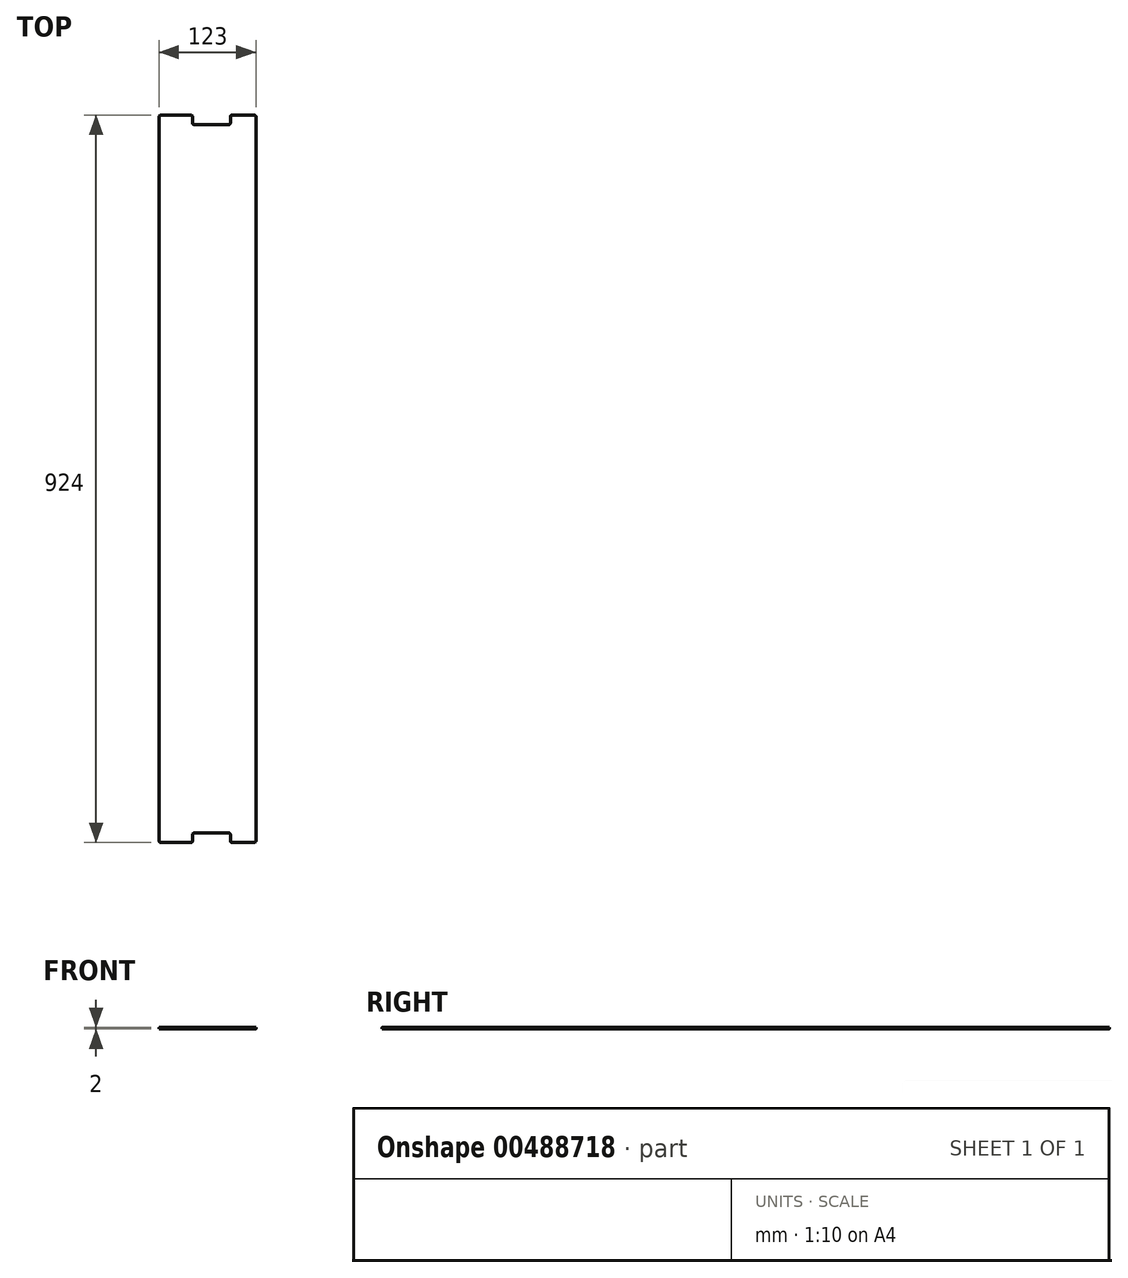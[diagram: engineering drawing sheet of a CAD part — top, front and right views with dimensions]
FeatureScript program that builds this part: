
annotation { "Feature Type Name" : "Feature", "Feature Type Description" : "" }
export const myFeature = defineFeature(function(context is Context, id is Id, definition is map)
    precondition{}
    {
        {
            var Q0;
            Q0=qCreatedBy(makeId("Top.planeOp"),FACE);
            var sketch = newSketch(context, id + "F0", { "sketchPlane" : qUnion([Q0])});
            skPoint(sketch, "E0.middle", {"position": v(0, 0) * mm});
            skLineSegment(sketch, "E1.bottom", {"start": v(24, 450) * mm, "end": v(-24, 450) * mm});
            skLineSegment(sketch, "E1.top", {"start": v(24, -450) * mm, "end": v(-24, -450) * mm});
            skLineSegment(sketch, "E1.left", {"start": v(24, 450) * mm, "end": v(24, -450) * mm});
            skLineSegment(sketch, "E1.right", {"start": v(-24, 450) * mm, "end": v(-24, -450) * mm});
            skLineSegment(sketch, "E2", {"start": v(-24, 450) * mm, "end": v(-24, 462) * mm});
            skLineSegment(sketch, "E3", {"start": v(-24, 462) * mm, "end": v(-66.5, 462) * mm});
            skLineSegment(sketch, "E4", {"start": v(-66.5, 462) * mm, "end": v(-66.5, -462) * mm});
            skLineSegment(sketch, "E5", {"start": v(24, 450) * mm, "end": v(24, 462) * mm});
            skLineSegment(sketch, "E6", {"start": v(24, 462) * mm, "end": v(56.5, 462) * mm});
            skLineSegment(sketch, "E7", {"start": v(56.5, 462) * mm, "end": v(56.5, -462) * mm});
            skLineSegment(sketch, "E8", {"start": v(56.5, -462) * mm, "end": v(24, -462) * mm});
            skLineSegment(sketch, "E9", {"start": v(24, -462) * mm, "end": v(24, -450) * mm});
            skLineSegment(sketch, "E10", {"start": v(-66.5, -462) * mm, "end": v(-24, -462) * mm});
            skLineSegment(sketch, "E11", {"start": v(-24, -462) * mm, "end": v(-24, -450) * mm});
            skSolve(sketch);
        }
        {
            var Q0;
            Q0=makeQuery(id+"F0.imprint","IMPRINT",FACE,{"disambiguationData":[TD([[makeQuery(id+"F0.imprint","IMPRINT",EDGE,{"derivedFrom":sQuery(id+"F0.wireOp",EDGE,"E1.bottom")}),1.0]])]});
            var Q1;
            Q1=makeQuery(id+"F0.imprint","IMPRINT",FACE,{"disambiguationData":[TD([[makeQuery(id+"F0.imprint","IMPRINT",EDGE,{"derivedFrom":sQuery(id+"F0.wireOp",EDGE,"E1.left")}),1.0]])]});
            var Q2;
            Q2=makeQuery(id+"F0.imprint","IMPRINT",FACE,{"disambiguationData":[TD([[makeQuery(id+"F0.imprint","IMPRINT",EDGE,{"derivedFrom":sQuery(id+"F0.wireOp",EDGE,"E1.right")}),-1.0]])]});
            extrude(context, id + "F1", {"entities" : qUnion([Q0, Q1, Q2]), "depth" : 2 * mm});
        }
        {
            assignVariable(context, id + "F2", {"name" : "fillet", "anyValue" : 2});
        }
        {
            var Q0;
            Q0=makeQuery(id+"F1.opExtrude","SWEPT_EDGE",EDGE,{"disambiguationData":[OSD([sQuery(id+"F0.wireOp",EDGE,"E4"),sQuery(id+"F0.wireOp",EDGE,"E10")])]});
            var Q1;
            Q1=makeQuery(id+"F1.opExtrude","SWEPT_EDGE",EDGE,{"disambiguationData":[OSD([sQuery(id+"F0.wireOp",EDGE,"E10"),sQuery(id+"F0.wireOp",EDGE,"E11")])]});
            var Q2;
            Q2=makeQuery(id+"F1.opExtrude","SWEPT_EDGE",EDGE,{"disambiguationData":[OSD([sQuery(id+"F0.wireOp",EDGE,"E1.top"),sQuery(id+"F0.wireOp",EDGE,"E1.right"),sQuery(id+"F0.wireOp",EDGE,"E11")])]});
            var Q3;
            Q3=makeQuery(id+"F1.opExtrude","SWEPT_EDGE",EDGE,{"disambiguationData":[OSD([sQuery(id+"F0.wireOp",EDGE,"E8"),sQuery(id+"F0.wireOp",EDGE,"E9")])]});
            var Q4;
            Q4=makeQuery(id+"F1.opExtrude","SWEPT_EDGE",EDGE,{"disambiguationData":[OSD([sQuery(id+"F0.wireOp",EDGE,"E7"),sQuery(id+"F0.wireOp",EDGE,"E8")])]});
            var Q5;
            Q5=makeQuery(id+"F1.opExtrude","SWEPT_EDGE",EDGE,{"disambiguationData":[OSD([sQuery(id+"F0.wireOp",EDGE,"E1.top"),sQuery(id+"F0.wireOp",EDGE,"E1.left"),sQuery(id+"F0.wireOp",EDGE,"E9")])]});
            var Q6;
            Q6=makeQuery(id+"F1.opExtrude","SWEPT_EDGE",EDGE,{"disambiguationData":[OSD([sQuery(id+"F0.wireOp",EDGE,"E6"),sQuery(id+"F0.wireOp",EDGE,"E7")])]});
            var Q7;
            Q7=makeQuery(id+"F1.opExtrude","SWEPT_EDGE",EDGE,{"disambiguationData":[OSD([sQuery(id+"F0.wireOp",EDGE,"E1.bottom"),sQuery(id+"F0.wireOp",EDGE,"E1.left"),sQuery(id+"F0.wireOp",EDGE,"E5")])]});
            var Q8;
            Q8=makeQuery(id+"F1.opExtrude","SWEPT_EDGE",EDGE,{"disambiguationData":[OSD([sQuery(id+"F0.wireOp",EDGE,"E5"),sQuery(id+"F0.wireOp",EDGE,"E6")])]});
            var Q9;
            Q9=makeQuery(id+"F1.opExtrude","SWEPT_EDGE",EDGE,{"disambiguationData":[OSD([sQuery(id+"F0.wireOp",EDGE,"E2"),sQuery(id+"F0.wireOp",EDGE,"E3")])]});
            var Q10;
            Q10=makeQuery(id+"F1.opExtrude","SWEPT_EDGE",EDGE,{"disambiguationData":[OSD([sQuery(id+"F0.wireOp",EDGE,"E3"),sQuery(id+"F0.wireOp",EDGE,"E4")])]});
            var Q11;
            Q11=makeQuery(id+"F1.opExtrude","SWEPT_EDGE",EDGE,{"disambiguationData":[OSD([sQuery(id+"F0.wireOp",EDGE,"E1.bottom"),sQuery(id+"F0.wireOp",EDGE,"E1.right"),sQuery(id+"F0.wireOp",EDGE,"E2")])]});
            fillet(context, id + "F3", {"entities" : qUnion([Q0, Q1, Q2, Q3, Q4, Q5, Q6, Q7, Q8, Q9, Q10, Q11]), "radius" : (getVariable(context, 'fillet')) * mm, "tangentPropagation" : true, "allowEdgeOverflow" : false});
        }
    });
